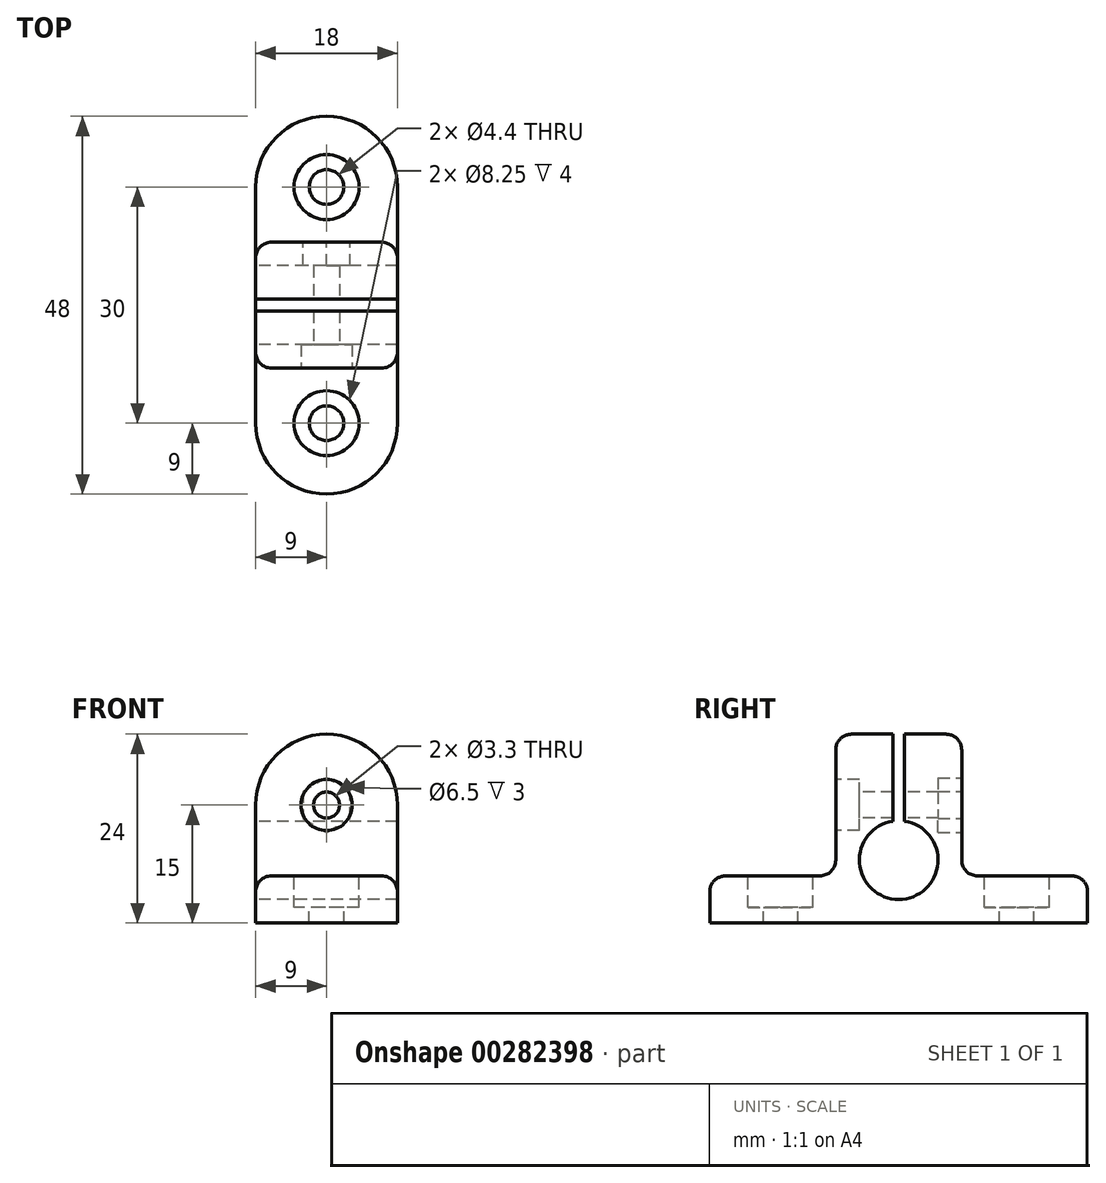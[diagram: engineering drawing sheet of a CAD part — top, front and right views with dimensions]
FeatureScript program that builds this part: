
annotation { "Feature Type Name" : "Feature", "Feature Type Description" : "" }
export const myFeature = defineFeature(function(context is Context, id is Id, definition is map)
    precondition{}
    {
        {
            var Q0;
            Q0=qCreatedBy(makeId("Right.planeOp"),FACE);
            var sketch = newSketch(context, id + "F0", { "sketchPlane" : qUnion([Q0])});
            skLineSegment(sketch, "E0", {"start": v(0, 0) * mm, "end": v(0, 6) * mm});
            skLineSegment(sketch, "E1", {"start": v(0, 6) * mm, "end": v(14, 6) * mm});
            skLineSegment(sketch, "E2", {"start": v(16, 8) * mm, "end": v(16, 24) * mm});
            skLineSegment(sketch, "E3", {"start": v(16, 24) * mm, "end": v(23.25, 24) * mm});
            skLineSegment(sketch, "E4", {"start": v(32, 24) * mm, "end": v(32, 8) * mm});
            skLineSegment(sketch, "E5", {"start": v(34, 6) * mm, "end": v(48, 6) * mm});
            skLineSegment(sketch, "E6", {"start": v(48, 6) * mm, "end": v(48, 0) * mm});
            skLineSegment(sketch, "E7", {"start": v(48, 0) * mm, "end": v(0, 0) * mm});
            skLineSegment(sketch, "E8", {"start": v(24, 0) * mm, "end": v(24, 24) * mm, "construction": true});
            skArc(sketch, "E9", {"start": v(23.25, 12.94) * mm, "mid": v(24, 3) * mm, "end": v(24.75, 12.94) * mm});
            skPoint(sketch, "E10.visualSharp", {"position": v(16, 6) * mm});
            skArc(sketch, "E10.filletArc", {"start": v(14, 6) * mm, "mid": v(15.41, 6.59) * mm, "end": v(16, 8) * mm});
            skPoint(sketch, "E11.visualSharp", {"position": v(32, 6) * mm});
            skArc(sketch, "E11.filletArc", {"start": v(32, 8) * mm, "mid": v(32.59, 6.59) * mm, "end": v(34, 6) * mm});
            skLineSegment(sketch, "E12.trimOffspring", {"start": v(24.75, 24) * mm, "end": v(32, 24) * mm});
            skLineSegment(sketch, "E13.trimOffspring", {"start": v(23.25, 12.94) * mm, "end": v(23.25, 24) * mm});
            skLineSegment(sketch, "E14.trimOffspring", {"start": v(24.75, 12.94) * mm, "end": v(24.75, 24) * mm});
            skSolve(sketch);
        }
        {
            var Q0;
            Q0=qSketchRegion(id+"F0",true);
            extrude(context, id + "F1", {"entities" : qUnion([Q0]), "depth" : 18 * mm});
        }
        {
            var Q0;
            Q0=makeQuery(id+"F1.opExtrude","SWEPT_FACE",FACE,{"disambiguationData":[OSD([sQuery(id+"F0.wireOp",EDGE,"E2")])]});
            var sketch = newSketch(context, id + "F2", { "sketchPlane" : qUnion([Q0])});
            skLineSegment(sketch, "E15", {"start": v(9, 24) * mm, "end": v(9, 8) * mm, "construction": true});
            skPoint(sketch, "E16", {"position": v(9, 15) * mm});
            skSolve(sketch);
        }
        {
            var Q0;
            Q0=makeQuery(id+"F1.opExtrude","SWEPT_FACE",FACE,{"disambiguationData":[OSD([sQuery(id+"F0.wireOp",EDGE,"E1")])]});
            var sketch = newSketch(context, id + "F3", { "sketchPlane" : qUnion([Q0])});
            skLineSegment(sketch, "E17", {"start": v(9, 0) * mm, "end": v(9, 40) * mm, "construction": true});
            skPoint(sketch, "E18", {"position": v(9, 9) * mm});
            skPoint(sketch, "E19", {"position": v(9, 39) * mm});
            skSolve(sketch);
        }
        {
            var Q0;
            Q0=sQuery(id+"F3.wireOp",VERTEX,"E18");
            var Q1;
            Q1=sQuery(id+"F3.wireOp",VERTEX,"E19");
            var Q2;
            Q2=makeQuery(id+"F1.opExtrude","SWEPT_BODY",BODY,{"disambiguationData":[OSD([sQuery(id+"F0.wireOp",EDGE,"E0"),sQuery(id+"F0.wireOp",EDGE,"E1"),sQuery(id+"F0.wireOp",EDGE,"E2"),sQuery(id+"F0.wireOp",EDGE,"E3"),sQuery(id+"F0.wireOp",EDGE,"E4"),sQuery(id+"F0.wireOp",EDGE,"E5"),sQuery(id+"F0.wireOp",EDGE,"E6"),sQuery(id+"F0.wireOp",EDGE,"E7"),sQuery(id+"F0.wireOp",EDGE,"E9"),sQuery(id+"F0.wireOp",EDGE,"E10.filletArc"),sQuery(id+"F0.wireOp",EDGE,"E11.filletArc"),sQuery(id+"F0.wireOp",EDGE,"E12.trimOffspring"),sQuery(id+"F0.wireOp",EDGE,"E13.trimOffspring"),sQuery(id+"F0.wireOp",EDGE,"E14.trimOffspring")])]});
            hole(context, id + "F4", {"style" : HoleStyle.C_BORE, "endStyle" : HoleEndStyle.THROUGH, "standardTappedOrClearance" : lookupTablePath({ "standard" : "ISO", "fit" : "Normal", "size" : "M4", "type" : "Clearance" }), "standardBlindInLast" : lookupTablePath({ "fit" : "Standard", "standard" : "ISO", "size" : "M4", "type" : "Clearance" }), "holeDiameter" : 4.4 * mm, "cBoreDiameter" : 8.25 * mm, "cBoreDepth" : 4 * mm, "tappedDepth" : 3 * mm, "tapClearance" : 3, "startFromSketch" : true, "locations" : qUnion([Q0, Q1]), "scope" : qUnion([Q2])});
        }
        {
            var Q0;
            Q0=makeQuery(id+"F1.opExtrude","CAP_EDGE",EDGE,{"disambiguationData":[OSD([sQuery(id+"F0.wireOp",EDGE,"E0")])],"isStart":false});
            var Q1;
            Q1=makeQuery(id+"F1.opExtrude","CAP_EDGE",EDGE,{"disambiguationData":[OSD([sQuery(id+"F0.wireOp",EDGE,"E0")])],"isStart":true});
            var Q2;
            Q2=makeQuery(id+"F1.opExtrude","CAP_EDGE",EDGE,{"disambiguationData":[OSD([sQuery(id+"F0.wireOp",EDGE,"E6")])],"isStart":false});
            var Q3;
            Q3=makeQuery(id+"F1.opExtrude","CAP_EDGE",EDGE,{"disambiguationData":[OSD([sQuery(id+"F0.wireOp",EDGE,"E6")])],"isStart":true});
            var Q4;
            Q4=makeQuery(id+"F1.opExtrude","CAP_EDGE",EDGE,{"disambiguationData":[OSD([sQuery(id+"F0.wireOp",EDGE,"E12.trimOffspring")])],"isStart":true});
            var Q5;
            Q5=makeQuery(id+"F1.opExtrude","CAP_EDGE",EDGE,{"disambiguationData":[OSD([sQuery(id+"F0.wireOp",EDGE,"E3")])],"isStart":true});
            var Q6;
            Q6=makeQuery(id+"F1.opExtrude","CAP_EDGE",EDGE,{"disambiguationData":[OSD([sQuery(id+"F0.wireOp",EDGE,"E3")])],"isStart":false});
            var Q7;
            Q7=makeQuery(id+"F1.opExtrude","CAP_EDGE",EDGE,{"disambiguationData":[OSD([sQuery(id+"F0.wireOp",EDGE,"E12.trimOffspring")])],"isStart":false});
            fillet(context, id + "F5", {"entities" : qUnion([Q0, Q1, Q2, Q3, Q4, Q5, Q6, Q7]), "radius" : 9 * mm, "tangentPropagation" : true, "allowEdgeOverflow" : false});
        }
        {
            var Q0;
            Q0=makeQuery(id+"F1.opExtrude","CAP_EDGE",EDGE,{"disambiguationData":[OSD([sQuery(id+"F0.wireOp",EDGE,"E1")])],"isStart":false});
            var Q1;
            Q1=makeQuery(id+"F1.opExtrude","CAP_EDGE",EDGE,{"disambiguationData":[OSD([sQuery(id+"F0.wireOp",EDGE,"E5")])],"isStart":false});
            fillet(context, id + "F6", {"entities" : qUnion([Q0, Q1]), "radius" : 2 * mm, "tangentPropagation" : true, "allowEdgeOverflow" : false});
        }
        {
            var Q0;
            Q0=sQuery(id+"F2.wireOp",VERTEX,"E16");
            var Q1;
            Q1=makeQuery(id+"F1.opExtrude","SWEPT_BODY",BODY,{"disambiguationData":[OSD([sQuery(id+"F0.wireOp",EDGE,"E0"),sQuery(id+"F0.wireOp",EDGE,"E1"),sQuery(id+"F0.wireOp",EDGE,"E2"),sQuery(id+"F0.wireOp",EDGE,"E3"),sQuery(id+"F0.wireOp",EDGE,"E4"),sQuery(id+"F0.wireOp",EDGE,"E5"),sQuery(id+"F0.wireOp",EDGE,"E6"),sQuery(id+"F0.wireOp",EDGE,"E7"),sQuery(id+"F0.wireOp",EDGE,"E9"),sQuery(id+"F0.wireOp",EDGE,"E10.filletArc"),sQuery(id+"F0.wireOp",EDGE,"E11.filletArc"),sQuery(id+"F0.wireOp",EDGE,"E12.trimOffspring"),sQuery(id+"F0.wireOp",EDGE,"E13.trimOffspring"),sQuery(id+"F0.wireOp",EDGE,"E14.trimOffspring")])]});
            hole(context, id + "F7", {"style" : HoleStyle.C_BORE, "endStyle" : HoleEndStyle.THROUGH, "standardTappedOrClearance" : lookupTablePath({ "standard" : "ISO", "fit" : "Normal", "size" : "M3", "type" : "Clearance" }), "standardBlindInLast" : lookupTablePath({ "fit" : "Standard", "standard" : "ISO", "size" : "M3", "type" : "Clearance" }), "holeDiameter" : 3.3 * mm, "cBoreDiameter" : 6.5 * mm, "cBoreDepth" : 3 * mm, "tappedDepth" : 3 * mm, "tapClearance" : 3, "startFromSketch" : true, "locations" : qUnion([Q0]), "scope" : qUnion([Q1])});
        }
        {
            var Q0;
            Q0=makeQuery(id+"F1.opExtrude","SWEPT_FACE",FACE,{"disambiguationData":[OSD([sQuery(id+"F0.wireOp",EDGE,"E4")])]});
            var sketch = newSketch(context, id + "F8", { "sketchPlane" : qUnion([Q0])});
            skCircle(sketch, "E20.cCircle", {"center": v(-9, 15) * mm, "radius": 3 * mm, "construction": true});
            skLineSegment(sketch, "E20.0", {"start": v(-6, 16.73) * mm, "end": v(-6, 13.27) * mm});
            skLineSegment(sketch, "E20.1", {"start": v(-6, 13.27) * mm, "end": v(-9, 11.54) * mm});
            skLineSegment(sketch, "E20.2", {"start": v(-9, 11.54) * mm, "end": v(-12, 13.27) * mm});
            skLineSegment(sketch, "E20.3", {"start": v(-12, 13.27) * mm, "end": v(-12, 16.73) * mm});
            skLineSegment(sketch, "E20.4", {"start": v(-12, 16.73) * mm, "end": v(-9, 18.46) * mm});
            skLineSegment(sketch, "E20.5", {"start": v(-9, 18.46) * mm, "end": v(-6, 16.73) * mm});
            skPoint(sketch, "E20.0.midPoint", {"position": v(-6, 15) * mm});
            skSolve(sketch);
        }
        {
            var Q0;
            Q0=qSketchRegion(id+"F8",true);
            extrude(context, id + "F9", {"entities" : qUnion([Q0]), "operationType" : NewBodyOperationType.REMOVE, "oppositeDirection" : true, "depth" : 3 * mm});
        }
    });
